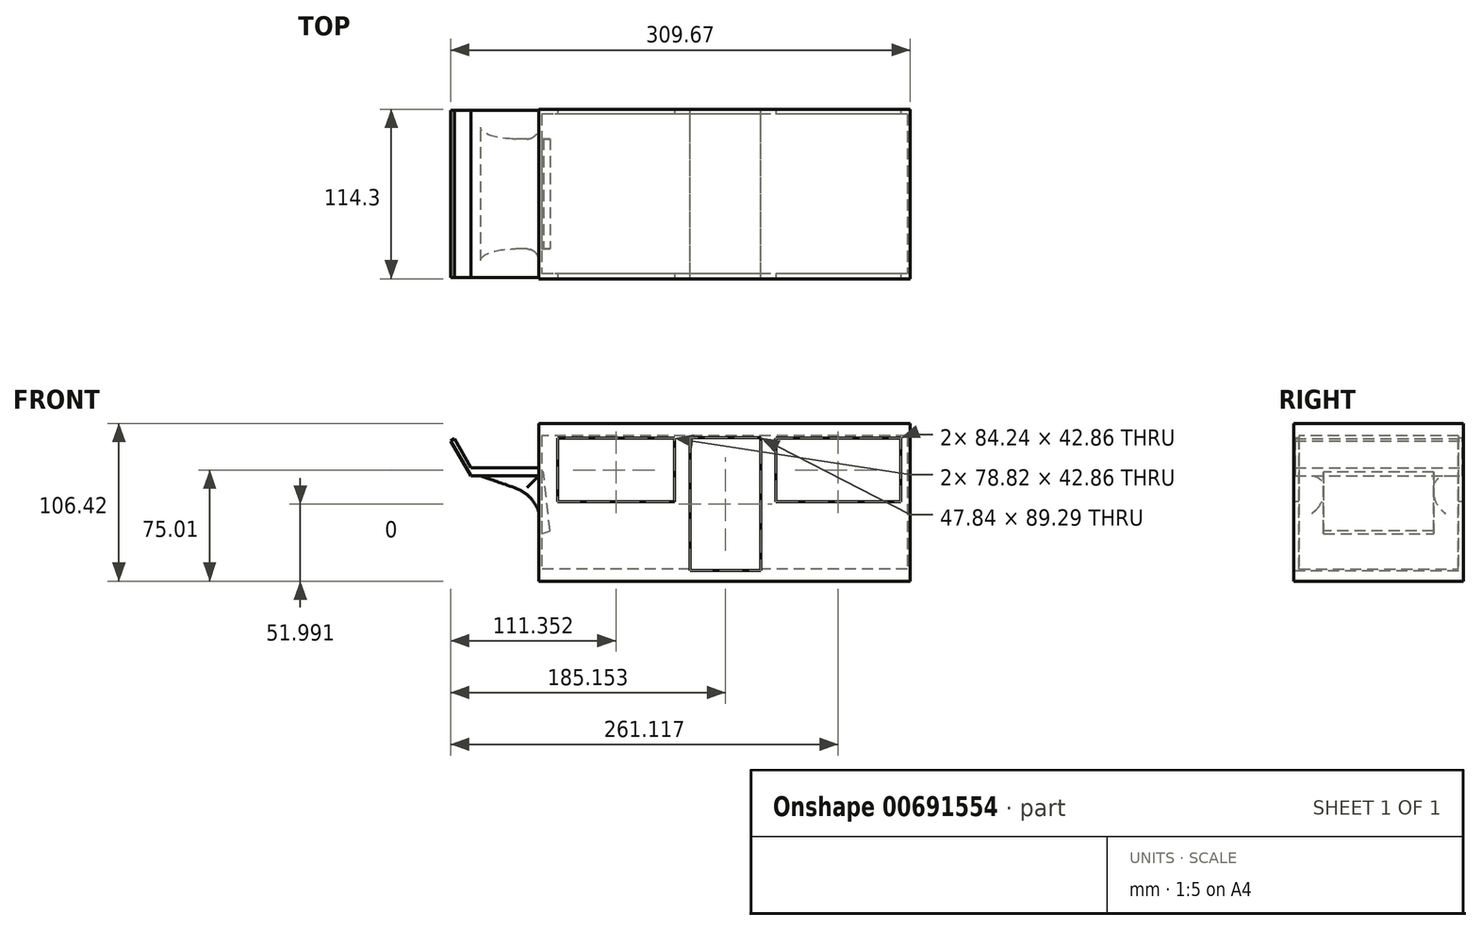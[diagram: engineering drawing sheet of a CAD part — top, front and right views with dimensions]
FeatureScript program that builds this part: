
annotation { "Feature Type Name" : "Feature", "Feature Type Description" : "" }
export const myFeature = defineFeature(function(context is Context, id is Id, definition is map)
    precondition{}
    {
        {
            var Q0;
            Q0=qCreatedBy(makeId("Front.planeOp"),FACE);
            var sketch = newSketch(context, id + "F0", { "sketchPlane" : qUnion([Q0])});
            skLineSegment(sketch, "E0.bottom", {"start": v(125.16, 53.2) * mm, "end": v(-125.16, 53.2) * mm});
            skLineSegment(sketch, "E0.top", {"start": v(125.16, -53.2) * mm, "end": v(-125.16, -53.2) * mm});
            skLineSegment(sketch, "E0.left", {"start": v(125.16, 53.2) * mm, "end": v(125.16, -53.2) * mm});
            skLineSegment(sketch, "E0.right", {"start": v(-125.16, 53.2) * mm, "end": v(-125.16, -53.2) * mm});
            skPoint(sketch, "E0.middle", {"position": v(0, 0) * mm});
            skSolve(sketch);
        }
        {
            var Q0;
            Q0 = qSketchRegion(id + "F0", true);
            extrude(context, id + "F1", {"entities" : qUnion([Q0]), "endBound" : BoundingType.SYMMETRIC, "depth" : 114.3 * mm, "offsetDistance" : 25.4 * mm});
        }
        {
            var Q0;
            Q0=qCreatedBy(makeId("Top.planeOp"),FACE);
            var sketch = newSketch(context, id + "F2", { "sketchPlane" : qUnion([Q0])});
            skLineSegment(sketch, "E1.bottom", {"start": v(123.09, 53.76) * mm, "end": v(-123.09, 53.76) * mm});
            skLineSegment(sketch, "E1.top", {"start": v(123.09, -53.76) * mm, "end": v(-123.09, -53.76) * mm});
            skLineSegment(sketch, "E1.left", {"start": v(123.09, 53.76) * mm, "end": v(123.09, -53.76) * mm});
            skLineSegment(sketch, "E1.right", {"start": v(-123.09, 53.76) * mm, "end": v(-123.09, -53.76) * mm});
            skPoint(sketch, "E1.middle", {"position": v(0, 0) * mm});
            skSolve(sketch);
        }
        {
            var Q0;
            Q0 = qSketchRegion(id + "F2", true);
            extrude(context, id + "F3", {"entities" : qUnion([Q0]), "operationType" : NewBodyOperationType.REMOVE, "endBound" : BoundingType.SYMMETRIC, "depth" : 89.92 * mm, "offsetDistance" : 25.4 * mm});
        }
        {
            var Q0;
            Q0=qCreatedBy(makeId("Front.planeOp"),FACE);
            var sketch = newSketch(context, id + "F4", { "sketchPlane" : qUnion([Q0])});
            skLineSegment(sketch, "E2.bottom", {"start": v(-33.75, 43.23) * mm, "end": v(-112.57, 43.23) * mm});
            skLineSegment(sketch, "E2.top", {"start": v(-33.75, 0.37) * mm, "end": v(-112.57, 0.37) * mm});
            skLineSegment(sketch, "E2.left", {"start": v(-33.75, 43.23) * mm, "end": v(-33.75, 0.37) * mm});
            skLineSegment(sketch, "E2.right", {"start": v(-112.57, 43.23) * mm, "end": v(-112.57, 0.37) * mm});
            skPoint(sketch, "E2.middle", {"position": v(-73.16, 21.8) * mm});
            skLineSegment(sketch, "E3.bottom", {"start": v(118.73, 43.23) * mm, "end": v(34.49, 43.23) * mm});
            skLineSegment(sketch, "E3.top", {"start": v(118.73, 0.37) * mm, "end": v(34.49, 0.37) * mm});
            skLineSegment(sketch, "E3.left", {"start": v(118.73, 43.23) * mm, "end": v(118.73, 0.37) * mm});
            skLineSegment(sketch, "E3.right", {"start": v(34.49, 43.23) * mm, "end": v(34.49, 0.37) * mm});
            skPoint(sketch, "E3.middle", {"position": v(76.6, 21.8) * mm});
            skSolve(sketch);
        }
        {
            var Q0;
            Q0 = qSketchRegion(id + "F4", true);
            extrude(context, id + "F5", {"entities" : qUnion([Q0]), "operationType" : NewBodyOperationType.REMOVE, "endBound" : BoundingType.SYMMETRIC, "oppositeDirection" : true, "depth" : 415.04 * mm, "offsetDistance" : 25.4 * mm});
        }
        {
            var Q0;
            Q0=qCreatedBy(makeId("Front.planeOp"),FACE);
            var sketch = newSketch(context, id + "F6", { "sketchPlane" : qUnion([Q0])});
            skLineSegment(sketch, "E4.bottom", {"start": v(-123.6, 23.2) * mm, "end": v(-170.93, 23.2) * mm});
            skLineSegment(sketch, "E4.top", {"start": v(-123.6, 17.8) * mm, "end": v(-170.93, 17.8) * mm});
            skLineSegment(sketch, "E4.left", {"start": v(-123.6, 23.2) * mm, "end": v(-123.6, 17.8) * mm});
            skLineSegment(sketch, "E4.right", {"start": v(-170.93, 23.2) * mm, "end": v(-170.93, 17.8) * mm});
            skLineSegment(sketch, "E5", {"start": v(-170.93, 17.8) * mm, "end": v(-184.51, 41.48) * mm});
            skLineSegment(sketch, "E6", {"start": v(-184.51, 41.48) * mm, "end": v(-182.1, 42.87) * mm});
            skLineSegment(sketch, "E7", {"start": v(-182.1, 42.87) * mm, "end": v(-170.93, 23.2) * mm});
            skSolve(sketch);
        }
        {
            var Q0;
            Q0 = qSketchRegion(id + "F6", true);
            extrude(context, id + "F7", {"entities" : qUnion([Q0]), "operationType" : NewBodyOperationType.ADD, "endBound" : BoundingType.SYMMETRIC, "depth" : 112.78 * mm, "offsetDistance" : 25.4 * mm});
        }
        {
            var Q0;
            Q0=qCreatedBy(makeId("Front.planeOp"),FACE);
            var sketch = newSketch(context, id + "F8", { "sketchPlane" : qUnion([Q0])});
            skLineSegment(sketch, "E8", {"start": v(-171.38, 20.26) * mm, "end": v(-140.9, 9.6) * mm});
            skArc(sketch, "E9", {"start": v(-125.06, -21.79) * mm, "mid": v(-126.65, -2.9) * mm, "end": v(-140.9, 9.6) * mm});
            skLineSegment(sketch, "E10", {"start": v(-125.06, -21.79) * mm, "end": v(-117.5, -19.35) * mm});
            skLineSegment(sketch, "E11", {"start": v(-117.5, -19.35) * mm, "end": v(-121.9, 20.35) * mm});
            skLineSegment(sketch, "E12", {"start": v(-121.9, 20.35) * mm, "end": v(-171.38, 20.26) * mm});
            skSolve(sketch);
        }
        {
            var Q0;
            Q0 = qSketchRegion(id + "F8", true);
            extrude(context, id + "F9", {"entities" : qUnion([Q0]), "operationType" : NewBodyOperationType.ADD, "endBound" : BoundingType.SYMMETRIC, "oppositeDirection" : true, "depth" : 74.17 * mm, "offsetDistance" : 25.4 * mm});
        }
        {
            var Q0;
            Q0=makeQuery(id+"F9.boolean.opBoolean","INTERSECT",EDGE,{"derivedFrom":[makeQuery(id+"F7.opExtrude","SWEPT_FACE",FACE,{"disambiguationData":[OSD([sQuery(id+"F6.wireOp",EDGE,"E4.top")])]}),makeQuery(id+"F9.opExtrude","CAP_FACE",FACE,{"disambiguationData":[OSD([sQuery(id+"F8.wireOp",EDGE,"E8"),sQuery(id+"F8.wireOp",EDGE,"E9"),sQuery(id+"F8.wireOp",EDGE,"E10"),sQuery(id+"F8.wireOp",EDGE,"E11"),sQuery(id+"F8.wireOp",EDGE,"E12")])],"isStart":false})]});
            var Q1;
            Q1=makeQuery(id+"F9.boolean.opBoolean","INTERSECT",EDGE,{"derivedFrom":[makeQuery(id+"F1.opExtrude","SWEPT_FACE",FACE,{"disambiguationData":[OSD([sQuery(id+"F0.wireOp",EDGE,"E0.right")])]}),makeQuery(id+"F9.opExtrude","CAP_FACE",FACE,{"disambiguationData":[OSD([sQuery(id+"F8.wireOp",EDGE,"E8"),sQuery(id+"F8.wireOp",EDGE,"E9"),sQuery(id+"F8.wireOp",EDGE,"E10"),sQuery(id+"F8.wireOp",EDGE,"E11"),sQuery(id+"F8.wireOp",EDGE,"E12")])],"isStart":false})]});
            var Q2;
            Q2=makeQuery(id+"F9.boolean.opBoolean","INTERSECT",EDGE,{"derivedFrom":[makeQuery(id+"F1.opExtrude","SWEPT_FACE",FACE,{"disambiguationData":[OSD([sQuery(id+"F0.wireOp",EDGE,"E0.right")])]}),makeQuery(id+"F9.opExtrude","CAP_FACE",FACE,{"disambiguationData":[OSD([sQuery(id+"F8.wireOp",EDGE,"E8"),sQuery(id+"F8.wireOp",EDGE,"E9"),sQuery(id+"F8.wireOp",EDGE,"E10"),sQuery(id+"F8.wireOp",EDGE,"E11"),sQuery(id+"F8.wireOp",EDGE,"E12")])],"isStart":true})]});
            var Q3;
            Q3=makeQuery(id+"F9.boolean.opBoolean","INTERSECT",EDGE,{"derivedFrom":[makeQuery(id+"F7.opExtrude","SWEPT_FACE",FACE,{"disambiguationData":[OSD([sQuery(id+"F6.wireOp",EDGE,"E4.top")])]}),makeQuery(id+"F9.opExtrude","CAP_FACE",FACE,{"disambiguationData":[OSD([sQuery(id+"F8.wireOp",EDGE,"E8"),sQuery(id+"F8.wireOp",EDGE,"E9"),sQuery(id+"F8.wireOp",EDGE,"E10"),sQuery(id+"F8.wireOp",EDGE,"E11"),sQuery(id+"F8.wireOp",EDGE,"E12")])],"isStart":true})]});
            fillet(context, id + "F10", {"entities" : qUnion([Q0, Q1, Q2, Q3]), "radius" : 7.9 * mm, "tangentPropagation" : true, "allowEdgeOverflow" : false});
        }
        {
            var Q0;
            Q0=makeQuery(id+"F9.boolean.opBoolean","INTERSECT",EDGE,{"derivedFrom":[makeQuery(id+"F1.opExtrude","SWEPT_FACE",FACE,{"disambiguationData":[OSD([sQuery(id+"F0.wireOp",EDGE,"E0.right")])]}),makeQuery(id+"F9.opExtrude","SWEPT_FACE",FACE,{"disambiguationData":[OSD([sQuery(id+"F8.wireOp",EDGE,"E9")])]})]});
            fillet(context, id + "F11", {"entities" : qUnion([Q0]), "radius" : 6.2 * mm, "tangentPropagation" : true, "allowEdgeOverflow" : false});
        }
        {
            var Q0;
            Q0=qCreatedBy(makeId("Front.planeOp"),FACE);
            var sketch = newSketch(context, id + "F12", { "sketchPlane" : qUnion([Q0])});
            skLineSegment(sketch, "E13.bottom", {"start": v(-23.28, 43.42) * mm, "end": v(24.56, 43.42) * mm});
            skLineSegment(sketch, "E13.top", {"start": v(-23.28, -45.86) * mm, "end": v(24.56, -45.86) * mm});
            skLineSegment(sketch, "E13.left", {"start": v(-23.28, 43.42) * mm, "end": v(-23.28, -45.86) * mm});
            skLineSegment(sketch, "E13.right", {"start": v(24.56, 43.42) * mm, "end": v(24.56, -45.86) * mm});
            skSolve(sketch);
        }
        {
            var Q0;
            Q0 = qSketchRegion(id + "F12", true);
            extrude(context, id + "F13", {"entities" : qUnion([Q0]), "operationType" : NewBodyOperationType.REMOVE, "endBound" : BoundingType.SYMMETRIC, "depth" : 157.48 * mm, "offsetDistance" : 25.4 * mm});
        }
    });
